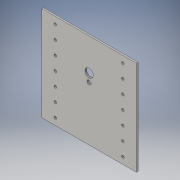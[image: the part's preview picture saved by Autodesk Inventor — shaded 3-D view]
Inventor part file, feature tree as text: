
AUTODESK INVENTOR PART (.ipt)
format: ipt  version: 2016 (Build 200138000, 138)  size: 175,616 bytes
history: native  units: in
note: dims shown in document units (in); Inventor stores cm internally (conversion verified against a paired STEP export)
features: sketch x5, projected_geometry x4, extrude x3, hole x1
ambient origin geometry x8: Origin, YZ Plane, XZ Plane, XY Plane, X Axis, Y Axis, Z Axis, Center Point
bodies: Solid1 (feature_tree)
feature tree (13):
  extrude  "Extrusion1"  Depth=7.0in
  extrude  "Extrusion2"  Depth=0.125in
  extrude  "Extrusion3"  Depth=2.0in
  sketch  "Sketch4"  dims[d7=0.75in d8=0.62in]
  sketch  "Sketch5"  dims[d9=1.0in d10=0.0in d11=0.8in d12=0.2in d13=0.308in d14=1.0in d15=0.0in d16=1.0in d17=1.0in d18=1.0in d19=1.0in d20=0.1875in d21=0.1875in d22=4.7244in d24=0.5in d25=0.3937in d27=1.0in d29=4.7244in d31=0.5in d32=0.3937in d34=1.0in d43=0.5in d44=0.5in d45=2.0in d46=2.0in d47=0.1875in d48=0.1875in d49=0.1875in d50=0.75in d51=0.375in d52=0.25in d53=0.5635in d54=1.0in d55=0.8108in]
  hole  "Hole2"  [1 undecoded]
  sketch  "Sketch1"  dims[d0=7.0in d1=7.0in]
  sketch  "Sketch2"  dims[d2=0.125in d3=0.0in d4=0.5in]
  projected_geometry  "Projected Loop1"
  sketch  "Sketch3"  dims[d5=0.5in d6=2.0in]
  projected_geometry  "Projected Loop2"
  projected_geometry  "Projected Loop3"
  projected_geometry  "Projected Loop4"
note: 1 required parameter value undecoded (feature->parameter linkage not recoverable at this tier; creation-order binding heuristic only, values carry confidence <= 0.55)
